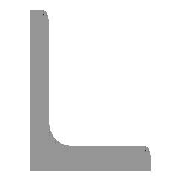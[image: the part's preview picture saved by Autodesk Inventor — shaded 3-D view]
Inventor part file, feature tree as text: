
AUTODESK INVENTOR PART (.ipt)
format: ipt  version: 2024.1 (Build 281209000, 209)  size: 120,320 bytes
history: native  units: mm (DEFAULTED — no unit token found)
features: other x4, sketch x1, plane x1
ambient origin geometry x8: Origin, YZ Plane, XZ Plane, XY Plane, X Axis, Y Axis, Z Axis, Center Point
bodies: Solid1 (feature_tree), Body (feature_tree)
feature tree (6):
  parser-record x1  (decoder bookkeeping rows leaked as tree rows — omitted from the tree; the rows remain in map.json)
  other  "Driven Length"
  other  "Start Plane"
  other  "End Plane"
  sketch  "Sketch3"  dims[d0=28.702mm d1=28.702mm d2=3.175mm d3=3.175mm d4=800.0mm d5=0.0mm d10=0.0mm d11=0.0mm d12=-0.0mm d13=800.0mm d14=2.286mm d15=1.27mm d16=90.0deg d17=800.0mm]
  plane  "Work Plane3"
